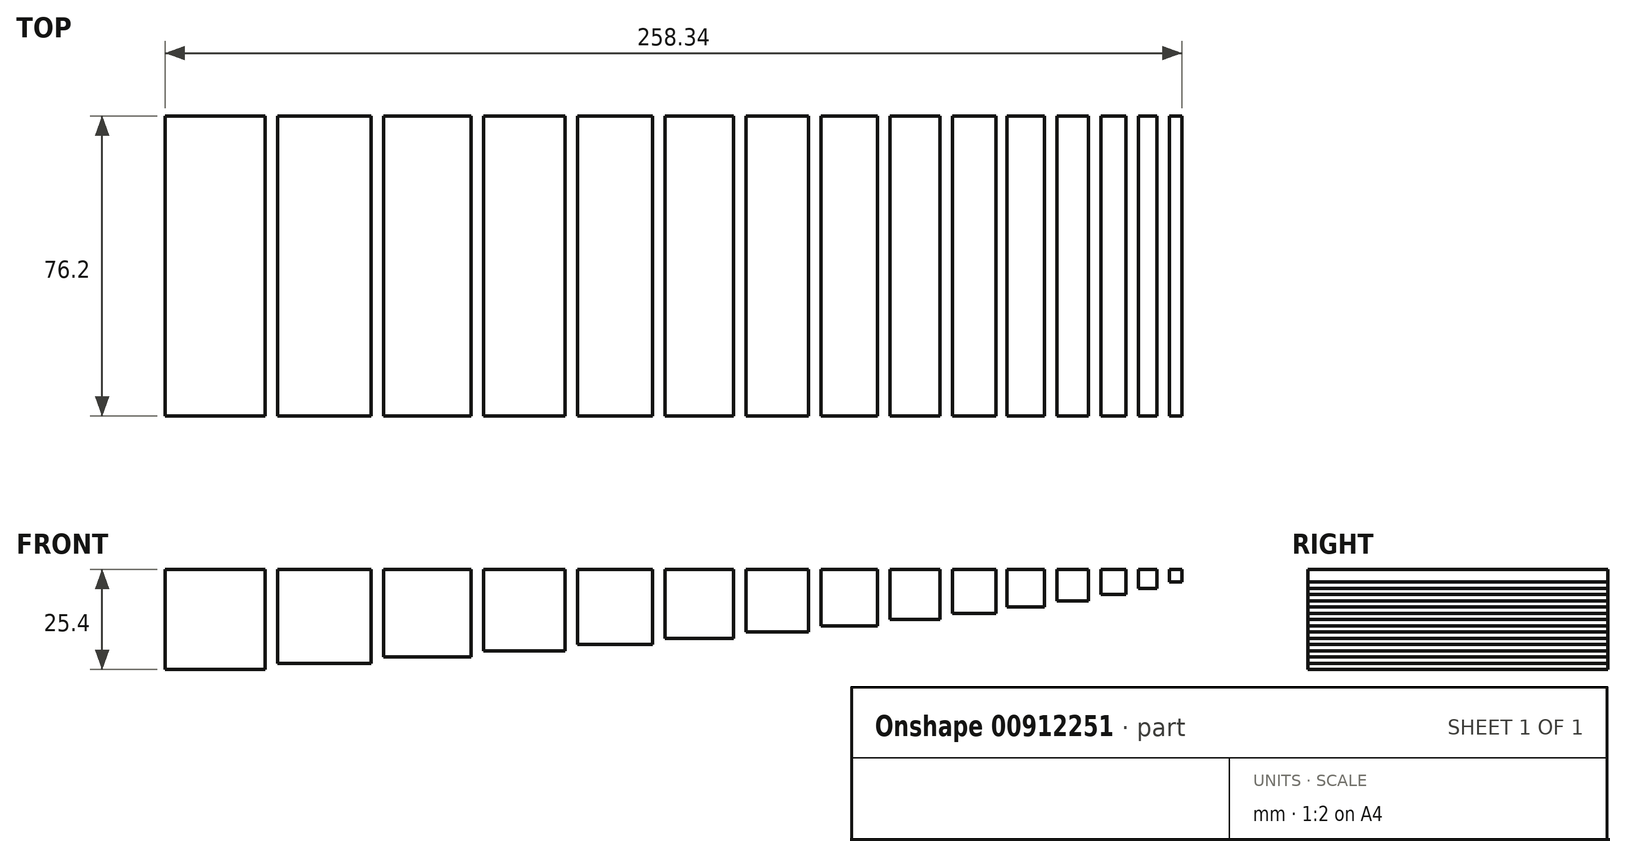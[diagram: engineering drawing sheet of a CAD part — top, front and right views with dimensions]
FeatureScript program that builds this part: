
annotation { "Feature Type Name" : "Feature", "Feature Type Description" : "" }
export const myFeature = defineFeature(function(context is Context, id is Id, definition is map)
    precondition{}
    {
        {
            var Q0;
            Q0=qCreatedBy(makeId("Front.planeOp"),FACE);
            var sketch = newSketch(context, id + "F0", { "sketchPlane" : qUnion([Q0])});
            skLineSegment(sketch, "E0.bottom", {"start": v(0, 0) * mm, "end": v(25.4, 0) * mm});
            skLineSegment(sketch, "E0.top", {"start": v(0, -25.4) * mm, "end": v(25.4, -25.4) * mm});
            skLineSegment(sketch, "E0.left", {"start": v(0, 0) * mm, "end": v(0, -25.4) * mm});
            skLineSegment(sketch, "E0.right", {"start": v(25.4, 0) * mm, "end": v(25.4, -25.4) * mm});
            skLineSegment(sketch, "E1.bottom", {"start": v(28.57, 0) * mm, "end": v(52.39, 0) * mm});
            skLineSegment(sketch, "E1.top", {"start": v(28.57, -23.81) * mm, "end": v(52.39, -23.81) * mm});
            skLineSegment(sketch, "E1.left", {"start": v(28.57, 0) * mm, "end": v(28.57, -23.81) * mm});
            skLineSegment(sketch, "E1.right", {"start": v(52.39, 0) * mm, "end": v(52.39, -23.81) * mm});
            skLineSegment(sketch, "E2.bottom", {"start": v(55.56, 0) * mm, "end": v(77.79, 0) * mm});
            skLineSegment(sketch, "E2.top", {"start": v(55.56, -22.22) * mm, "end": v(77.79, -22.22) * mm});
            skLineSegment(sketch, "E2.left", {"start": v(55.56, 0) * mm, "end": v(55.56, -22.22) * mm});
            skLineSegment(sketch, "E2.right", {"start": v(77.79, 0) * mm, "end": v(77.79, -22.22) * mm});
            skLineSegment(sketch, "E3.bottom", {"start": v(80.96, 0) * mm, "end": v(101.6, 0) * mm});
            skLineSegment(sketch, "E3.top", {"start": v(80.96, -20.64) * mm, "end": v(101.6, -20.64) * mm});
            skLineSegment(sketch, "E3.left", {"start": v(80.96, 0) * mm, "end": v(80.96, -20.64) * mm});
            skLineSegment(sketch, "E3.right", {"start": v(101.6, 0) * mm, "end": v(101.6, -20.64) * mm});
            skLineSegment(sketch, "E4.bottom", {"start": v(104.77, -19.05) * mm, "end": v(123.82, -19.05) * mm});
            skLineSegment(sketch, "E4.top", {"start": v(104.77, 0) * mm, "end": v(123.82, 0) * mm});
            skLineSegment(sketch, "E4.left", {"start": v(104.77, -19.05) * mm, "end": v(104.77, 0) * mm});
            skLineSegment(sketch, "E4.right", {"start": v(123.82, -19.05) * mm, "end": v(123.82, 0) * mm});
            skLineSegment(sketch, "E5.bottom", {"start": v(127, -17.46) * mm, "end": v(144.46, -17.46) * mm});
            skLineSegment(sketch, "E5.top", {"start": v(127, 0) * mm, "end": v(144.46, 0) * mm});
            skLineSegment(sketch, "E5.left", {"start": v(127, -17.46) * mm, "end": v(127, 0) * mm});
            skLineSegment(sketch, "E5.right", {"start": v(144.46, -17.46) * mm, "end": v(144.46, 0) * mm});
            skLineSegment(sketch, "E6.bottom", {"start": v(147.64, -15.88) * mm, "end": v(163.51, -15.88) * mm});
            skLineSegment(sketch, "E6.top", {"start": v(147.64, 0) * mm, "end": v(163.51, 0) * mm});
            skLineSegment(sketch, "E6.left", {"start": v(147.64, -15.88) * mm, "end": v(147.64, 0) * mm});
            skLineSegment(sketch, "E6.right", {"start": v(163.51, -15.88) * mm, "end": v(163.51, 0) * mm});
            skLineSegment(sketch, "E7.bottom", {"start": v(166.69, -14.29) * mm, "end": v(180.98, -14.29) * mm});
            skLineSegment(sketch, "E7.top", {"start": v(166.69, 0) * mm, "end": v(180.98, 0) * mm});
            skLineSegment(sketch, "E7.left", {"start": v(166.69, -14.29) * mm, "end": v(166.69, 0) * mm});
            skLineSegment(sketch, "E7.right", {"start": v(180.98, -14.29) * mm, "end": v(180.98, 0) * mm});
            skLineSegment(sketch, "E8.bottom", {"start": v(184.15, -12.7) * mm, "end": v(196.85, -12.7) * mm});
            skLineSegment(sketch, "E8.top", {"start": v(184.15, 0) * mm, "end": v(196.85, 0) * mm});
            skLineSegment(sketch, "E8.left", {"start": v(184.15, -12.7) * mm, "end": v(184.15, 0) * mm});
            skLineSegment(sketch, "E8.right", {"start": v(196.85, -12.7) * mm, "end": v(196.85, 0) * mm});
            skLineSegment(sketch, "E9.bottom", {"start": v(200.03, -11.11) * mm, "end": v(211.14, -11.11) * mm});
            skLineSegment(sketch, "E9.top", {"start": v(200.03, 0) * mm, "end": v(211.14, 0) * mm});
            skLineSegment(sketch, "E9.left", {"start": v(200.03, -11.11) * mm, "end": v(200.03, 0) * mm});
            skLineSegment(sketch, "E9.right", {"start": v(211.14, -11.11) * mm, "end": v(211.14, 0) * mm});
            skLineSegment(sketch, "E10.bottom", {"start": v(213.89, -9.53) * mm, "end": v(223.41, -9.53) * mm});
            skLineSegment(sketch, "E10.top", {"start": v(213.89, 0) * mm, "end": v(223.41, 0) * mm});
            skLineSegment(sketch, "E10.left", {"start": v(213.89, -9.53) * mm, "end": v(213.89, 0) * mm});
            skLineSegment(sketch, "E10.right", {"start": v(223.41, -9.53) * mm, "end": v(223.41, 0) * mm});
            skLineSegment(sketch, "E11.bottom", {"start": v(226.59, -7.94) * mm, "end": v(234.52, -7.94) * mm});
            skLineSegment(sketch, "E11.top", {"start": v(226.59, 0) * mm, "end": v(234.52, 0) * mm});
            skLineSegment(sketch, "E11.left", {"start": v(226.59, -7.94) * mm, "end": v(226.59, 0) * mm});
            skLineSegment(sketch, "E11.right", {"start": v(234.52, -7.94) * mm, "end": v(234.52, 0) * mm});
            skLineSegment(sketch, "E12.bottom", {"start": v(237.7, -6.35) * mm, "end": v(244.05, -6.35) * mm});
            skLineSegment(sketch, "E12.top", {"start": v(237.7, 0) * mm, "end": v(244.05, 0) * mm});
            skLineSegment(sketch, "E12.left", {"start": v(237.7, -6.35) * mm, "end": v(237.7, 0) * mm});
            skLineSegment(sketch, "E12.right", {"start": v(244.05, -6.35) * mm, "end": v(244.05, 0) * mm});
            skLineSegment(sketch, "E13.bottom", {"start": v(247.22, -4.76) * mm, "end": v(251.99, -4.76) * mm});
            skLineSegment(sketch, "E13.top", {"start": v(247.22, 0) * mm, "end": v(251.99, 0) * mm});
            skLineSegment(sketch, "E13.left", {"start": v(247.22, -4.76) * mm, "end": v(247.22, 0) * mm});
            skLineSegment(sketch, "E13.right", {"start": v(251.99, -4.76) * mm, "end": v(251.99, 0) * mm});
            skLineSegment(sketch, "E14.bottom", {"start": v(255.16, -3.17) * mm, "end": v(258.34, -3.17) * mm});
            skLineSegment(sketch, "E14.top", {"start": v(255.16, 0) * mm, "end": v(258.34, 0) * mm});
            skLineSegment(sketch, "E14.left", {"start": v(255.16, -3.17) * mm, "end": v(255.16, 0) * mm});
            skLineSegment(sketch, "E14.right", {"start": v(258.34, -3.17) * mm, "end": v(258.34, 0) * mm});
            skSolve(sketch);
        }
        {
            var Q0;
            Q0 = qSketchRegion(id + "F0", true);
            extrude(context, id + "F1", {"entities" : qUnion([Q0]), "depth" : 76.2 * mm, "offsetDistance" : 25.4 * mm});
        }
    });
